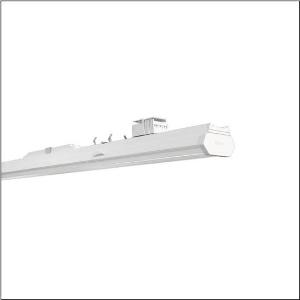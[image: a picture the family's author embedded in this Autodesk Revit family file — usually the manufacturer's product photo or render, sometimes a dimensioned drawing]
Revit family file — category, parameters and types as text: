
# Revit family: licross_r__11_protected_mo_51tp12cn49xg_4f1c
name_source: partatom
category: Lighting Fixtures
units: mm (PartAtom-declared; Revit-internal decimal feet)

## family parameters
Cut with Voids When Loaded = No
Host = Face
Light Source = No
Part Type = Normal
Room Calculation Point = No
Round Connector Dimension = Use Diameter
Shared = No

## types (1)
- --- (1 x LED, 9070 lm, 49.4 W, 4000K)
    Apparent Load = 49 VA
    CIE Flux Codes = 73 92 98 99 100
    Color Rendering = 80
    Color Temperature = 4000K
    Default Elevation = 1800 mm
    Description = Licross® 11 Protected MO, luminaire insert, of sheet steel, galvanised, coil coated, white, length: 1.500mm, width: 90mm, height: 101mm, LED rated luminous flux: 9.070lm, light colour: 840, control gear: ON/OFF Multilumen, CLOi, with plug, 3-pole, with phase selection, mains connection: 220..240V, AC, 50/60Hz, start of lifetime: 49W, end of service life: 55W, halogen-free wiring, primary light control with lens, of plastic, primary optical cover: cover, of PMMA, light emission: direct distribution, primary light characteristic: symmetric, protection rating (complete): IP64, insulation class (complete): insulation class I (protective earthing), certification: CE, ENEC, VDE, UKCA, protection symbol: D if used in an environment with conductive dust loads with corresponding accessories, impact resistance: IK06, permissible ambient temperature for indoor applications: -35..+40°C, corresponds to IFS (International Featured Standards) requirements for safety and quality in the food industry, reducing of maximum allowable ambient temperature of 5°C with ceiling mounting, LABS conformity tested according to VDMA 24364:2018-05, packaging unit: 1 piece
    Height = 92 mm
    Lamp = 1 x LED
    Lamp Light Flux = 9070 lm
    Lamp Power = 49.4 W
    Lamp count = 1
    Length = 1500 mm
    Luminous efficacy = 184 lm/W
    Manufacturer = Siteco
    ModVariant = No
    Model = 51TP12CN49XG
    Mounting Place = Ceiling
    Mounting Type = Pendant
    Number of Poles = 1
    OnlyDefault = Yes
    Power Factor = 1
    Product Name = Licross® 11 Protected MO
    Product group = luminaire insert
    ProductGroupID = 901
    Protection Class = Protection class I
    Protection Degree = IP 64
    RLX_Detail_Level = 1
    RLX_Emergency_Light_Flux = 0 lm
    RLX_Emergency_Type = 0
    RLX_Emergency_Type_DB = No
    RlxData = <blob elided: 22141 chars, md5=fc4cc6e2>
    Socket = socket
    Standby Power = 0 W
    System Light Flux = 9070 lm
    System Power = 49 W
    Type Comments = factory setting: luminous flux: 100 % | (A | C | E) | 113 mA
    Type Image = l_1256148.jpg
    URL = http://relux.com
    VarID = @adj_055235
    Voltage = 0 V
    Weight = 0.00 kg
    Width = 88 mm

## geometry (parser evidence)
native form markers: Blend x4, Sweep x11
no freeform markers — native parametric forms only
